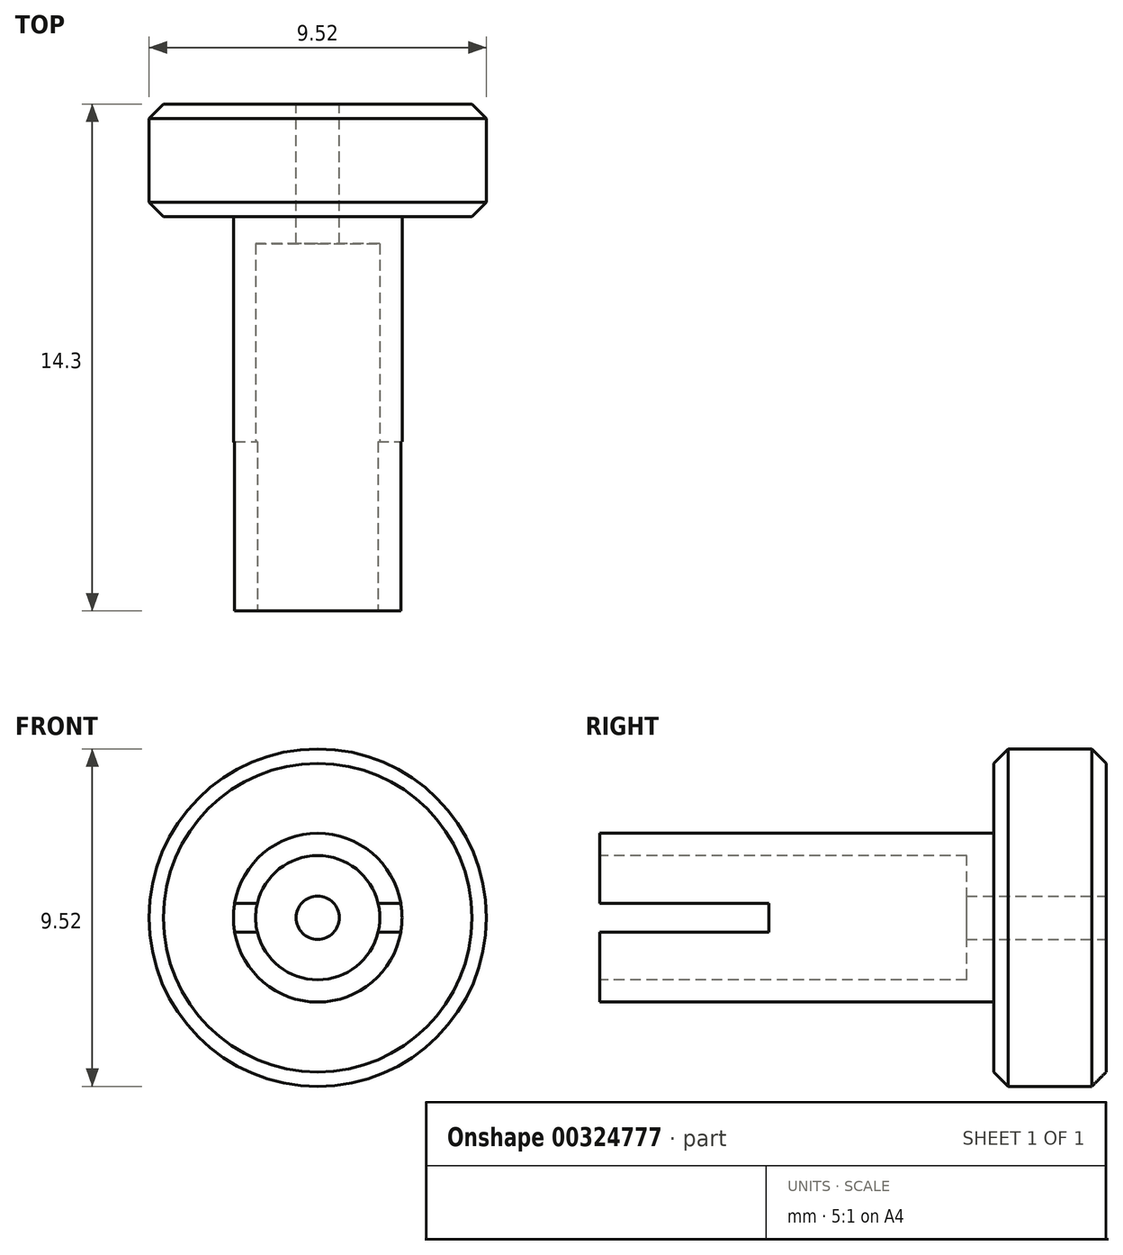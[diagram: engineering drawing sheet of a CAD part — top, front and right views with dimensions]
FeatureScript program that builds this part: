
annotation { "Feature Type Name" : "Feature", "Feature Type Description" : "" }
export const myFeature = defineFeature(function(context is Context, id is Id, definition is map)
    precondition{}
    {
        {
            var Q0;
            Q0=qCreatedBy(makeId("Front.planeOp"),FACE);
            var sketch = newSketch(context, id + "F0", { "sketchPlane" : qUnion([Q0])});
            skCircle(sketch, "E0", {"center": v(0, 0) * mm, "radius": 4.76 * mm});
            skSolve(sketch);
        }
        {
            var Q0;
            Q0=makeQuery(id+"F0.imprint","IMPRINT",FACE,{"disambiguationData":[TD([[makeQuery(id+"F0.imprint","IMPRINT",EDGE,{"derivedFrom":sQuery(id+"F0.wireOp",EDGE,"E0")}),1.0]])]});
            extrude(context, id + "F1", {"entities" : qUnion([Q0]), "depth" : 3.17 * mm, "offsetDistance" : 25.4 * mm});
        }
        {
            var Q0;
            Q0=makeQuery(id+"F1.opExtrude","CAP_FACE",FACE,{"disambiguationData":[OSD([sQuery(id+"F0.wireOp",EDGE,"E0")])],"isStart":false});
            var sketch = newSketch(context, id + "F2", { "sketchPlane" : qUnion([Q0])});
            skCircle(sketch, "E1", {"center": v(0, 0) * mm, "radius": 2.38 * mm});
            skSolve(sketch);
        }
        {
            var Q0;
            Q0=makeQuery(id+"F2.imprint","IMPRINT",FACE,{"disambiguationData":[TD([[makeQuery(id+"F2.imprint","IMPRINT",EDGE,{"derivedFrom":sQuery(id+"F2.wireOp",EDGE,"E1")}),1.0]])]});
            extrude(context, id + "F3", {"entities" : qUnion([Q0]), "operationType" : NewBodyOperationType.ADD, "depth" : 11.13 * mm, "offsetDistance" : 25.4 * mm});
        }
        {
            var Q0;
            Q0=makeQuery(id+"F3.opExtrude","CAP_FACE",FACE,{"disambiguationData":[OSD([sQuery(id+"F2.wireOp",EDGE,"E1")])],"isStart":false});
            var sketch = newSketch(context, id + "F4", { "sketchPlane" : qUnion([Q0])});
            skCircle(sketch, "E2", {"center": v(0, 0) * mm, "radius": 1.75 * mm});
            skSolve(sketch);
        }
        {
            var Q0;
            Q0=makeQuery(id+"F4.imprint","IMPRINT",FACE,{"disambiguationData":[TD([[makeQuery(id+"F4.imprint","IMPRINT",EDGE,{"derivedFrom":sQuery(id+"F4.wireOp",EDGE,"E2")}),1.0]])]});
            extrude(context, id + "F5", {"entities" : qUnion([Q0]), "operationType" : NewBodyOperationType.REMOVE, "oppositeDirection" : true, "depth" : 10.36 * mm, "offsetDistance" : 25.4 * mm});
        }
        {
            var Q0;
            Q0=makeQuery(id+"F1.opExtrude","CAP_FACE",FACE,{"disambiguationData":[OSD([sQuery(id+"F0.wireOp",EDGE,"E0")])],"isStart":true});
            var sketch = newSketch(context, id + "F6", { "sketchPlane" : qUnion([Q0])});
            skCircle(sketch, "E3", {"center": v(0, 0) * mm, "radius": 0.6 * mm});
            skSolve(sketch);
        }
        {
            var Q0;
            Q0=makeQuery(id+"F6.imprint","IMPRINT",FACE,{"disambiguationData":[TD([[makeQuery(id+"F6.imprint","IMPRINT",EDGE,{"derivedFrom":sQuery(id+"F6.wireOp",EDGE,"E3")}),1.0]])]});
            extrude(context, id + "F7", {"entities" : qUnion([Q0]), "operationType" : NewBodyOperationType.REMOVE, "endBound" : BoundingType.THROUGH_ALL, "oppositeDirection" : true, "depth" : 25.4 * mm, "offsetDistance" : 25.4 * mm});
        }
        {
            var Q0;
            Q0=makeQuery(id+"F1.opExtrude","CAP_EDGE",EDGE,{"disambiguationData":[OSD([sQuery(id+"F0.wireOp",EDGE,"E0")])],"isStart":true});
            var Q1;
            Q1=makeQuery(id+"F1.opExtrude","CAP_EDGE",EDGE,{"disambiguationData":[OSD([sQuery(id+"F0.wireOp",EDGE,"E0")])],"isStart":false});
            chamfer(context, id + "F8", {"entities" : qUnion([Q0, Q1]), "width" : 0.4 * mm, "tangentPropagation" : true});
        }
        {
            var Q0;
            Q0=qCreatedBy(makeId("Right.planeOp"),FACE);
            var sketch = newSketch(context, id + "F9", { "sketchPlane" : qUnion([Q0])});
            skLineSegment(sketch, "E4.bottom", {"start": v(-14.3, 0.4) * mm, "end": v(-9.53, 0.4) * mm});
            skLineSegment(sketch, "E4.top", {"start": v(-14.3, -0.4) * mm, "end": v(-9.53, -0.4) * mm});
            skLineSegment(sketch, "E4.left", {"start": v(-14.3, 0.4) * mm, "end": v(-14.3, -0.4) * mm});
            skLineSegment(sketch, "E4.right", {"start": v(-9.53, 0.4) * mm, "end": v(-9.53, -0.4) * mm});
            skSolve(sketch);
        }
        {
            var Q0;
            Q0=makeQuery(id+"F9.imprint","IMPRINT",FACE,{"disambiguationData":[TD([[makeQuery(id+"F9.imprint","IMPRINT",EDGE,{"derivedFrom":sQuery(id+"F9.wireOp",EDGE,"E4.bottom")}),-1.0]])]});
            extrude(context, id + "F10", {"entities" : qUnion([Q0]), "operationType" : NewBodyOperationType.REMOVE, "oppositeDirection" : true, "depth" : 25.4 * mm, "offsetDistance" : 25.4 * mm, "symmetric" : true});
        }
    });
